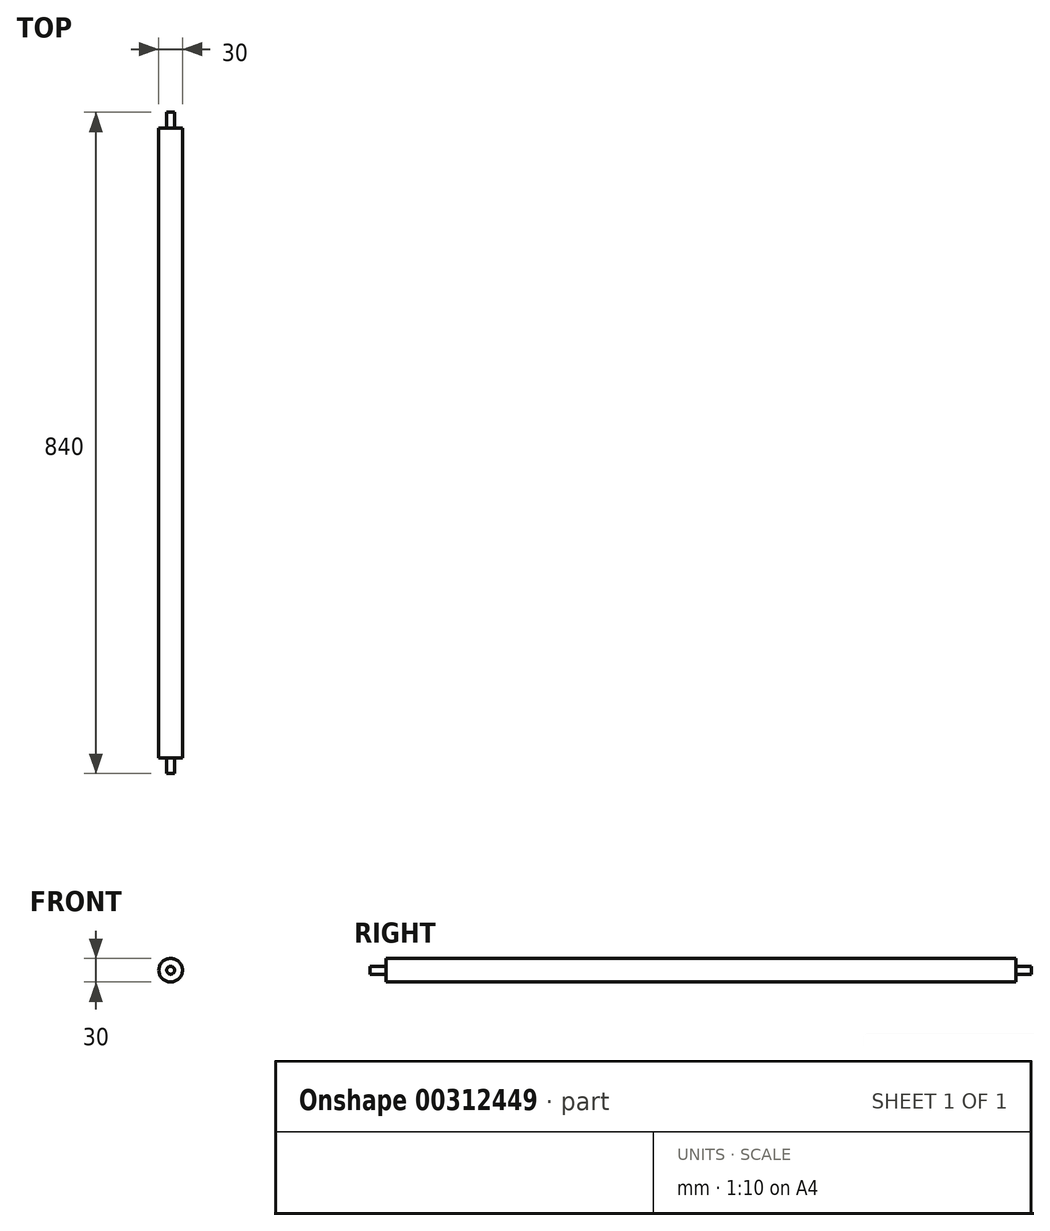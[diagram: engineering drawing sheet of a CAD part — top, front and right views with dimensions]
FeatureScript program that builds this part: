
annotation { "Feature Type Name" : "Feature", "Feature Type Description" : "" }
export const myFeature = defineFeature(function(context is Context, id is Id, definition is map)
    precondition{}
    {
        {
            var Q0;
            Q0=qCreatedBy(makeId("Front.planeOp"),FACE);
            var sketch = newSketch(context, id + "F0", { "sketchPlane" : qUnion([Q0])});
            skCircle(sketch, "E0", {"center": v(0, 0) * mm, "radius": 15 * mm});
            skCircle(sketch, "E1", {"center": v(0, 0) * mm, "radius": 5 * mm});
            skSolve(sketch);
        }
        {
            var Q0;
            Q0=makeQuery(id+"F0.imprint","IMPRINT",FACE,{"disambiguationData":[TD([[makeQuery(id+"F0.imprint","IMPRINT",EDGE,{"derivedFrom":sQuery(id+"F0.wireOp",EDGE,"E0")}),1.0]])]});
            var Q1;
            Q1=makeQuery(id+"F0.imprint","IMPRINT",FACE,{"disambiguationData":[TD([[makeQuery(id+"F0.imprint","IMPRINT",EDGE,{"derivedFrom":sQuery(id+"F0.wireOp",EDGE,"E1")}),1.0]])]});
            extrude(context, id + "F1", {"entities" : qUnion([Q0, Q1]), "depth" : 800 * mm});
        }
        {
            var Q0;
            Q0=makeQuery(id+"F0.imprint","IMPRINT",FACE,{"disambiguationData":[TD([[makeQuery(id+"F0.imprint","IMPRINT",EDGE,{"derivedFrom":sQuery(id+"F0.wireOp",EDGE,"E1")}),1.0]])]});
            extrude(context, id + "F2", {"entities" : qUnion([Q0]), "operationType" : NewBodyOperationType.ADD, "oppositeDirection" : true, "depth" : 20 * mm, "offsetDistance" : 25 * mm});
        }
        {
            var Q0;
            Q0=qCreatedBy(makeId("Front.planeOp"),FACE);
            cPlane(context, id + "F3", {"entities" : qUnion([Q0]), "cplaneType" : CPlaneType.OFFSET, "offset" : 800 * mm, "width" : 150 * mm, "height" : 150 * mm});
        }
        {
            var Q0;
            Q0=qCreatedBy(id+"F3.planeOp",FACE);
            var sketch = newSketch(context, id + "F4", { "sketchPlane" : qUnion([Q0])});
            skCircle(sketch, "E2", {"center": v(0, 0) * mm, "radius": 5 * mm});
            skSolve(sketch);
        }
        {
            var Q0;
            Q0=makeQuery(id+"F4.imprint","IMPRINT",FACE,{"disambiguationData":[TD([[makeQuery(id+"F4.imprint","IMPRINT",EDGE,{"derivedFrom":sQuery(id+"F4.wireOp",EDGE,"E2")}),1.0]])]});
            extrude(context, id + "F5", {"entities" : qUnion([Q0]), "operationType" : NewBodyOperationType.ADD, "depth" : 20 * mm, "offsetDistance" : 25 * mm});
        }
    });
